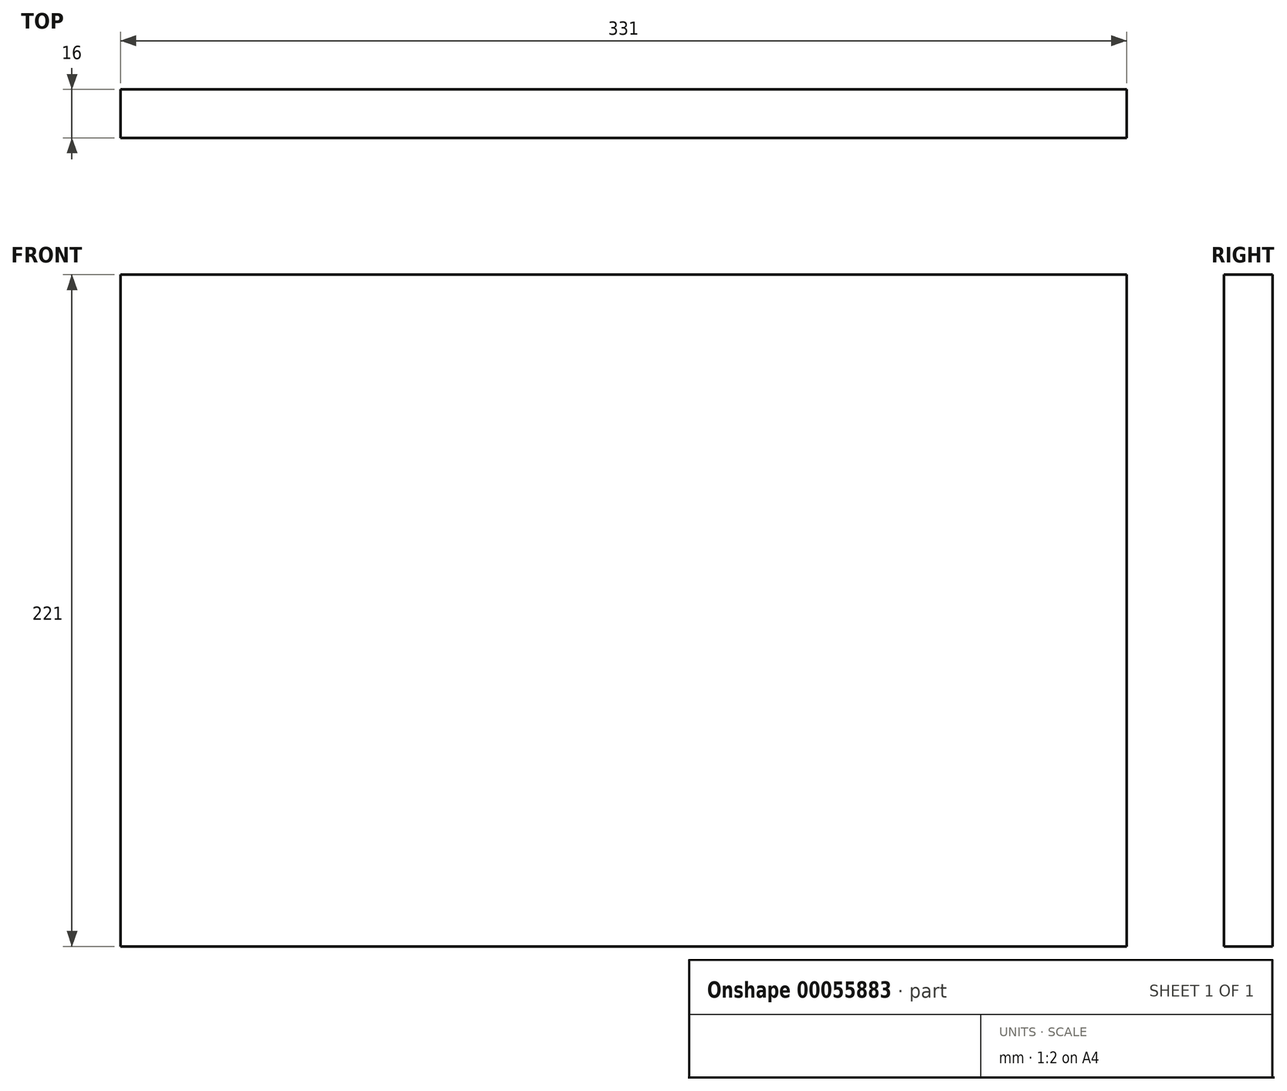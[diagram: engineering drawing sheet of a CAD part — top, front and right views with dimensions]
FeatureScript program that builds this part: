
annotation { "Feature Type Name" : "Feature", "Feature Type Description" : "" }
export const myFeature = defineFeature(function(context is Context, id is Id, definition is map)
    precondition{}
    {
        {
            var Q0;
            Q0=qCreatedBy(makeId("Front.planeOp"),FACE);
            var sketch = newSketch(context, id + "F0", { "sketchPlane" : qUnion([Q0])});
            skLineSegment(sketch, "E0.rect.bottom", {"start": v(-165.5, 110.5) * mm, "end": v(165.5, 110.5) * mm});
            skLineSegment(sketch, "E0.rect.top", {"start": v(-165.5, -110.5) * mm, "end": v(165.5, -110.5) * mm});
            skLineSegment(sketch, "E0.rect.left", {"start": v(-165.5, 110.5) * mm, "end": v(-165.5, -110.5) * mm});
            skLineSegment(sketch, "E0.rect.right", {"start": v(165.5, 110.5) * mm, "end": v(165.5, -110.5) * mm});
            skPoint(sketch, "E0.rect.middle", {"position": v(0, 0) * mm});
            skSolve(sketch);
        }
        {
            var Q0;
            Q0=makeQuery(id+"F0.imprint","IMPRINT",FACE,{"disambiguationData":[TD([[makeQuery(id+"F0.imprint","IMPRINT",EDGE,{"derivedFrom":sQuery(id+"F0.wireOp",EDGE,"E0.rect.bottom")}),-1.0]])]});
            extrude(context, id + "F1", {"entities" : qUnion([Q0]), "oppositeDirection" : true, "depth" : 16 * mm});
        }
    });
